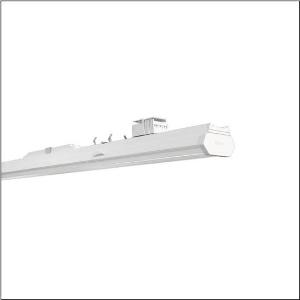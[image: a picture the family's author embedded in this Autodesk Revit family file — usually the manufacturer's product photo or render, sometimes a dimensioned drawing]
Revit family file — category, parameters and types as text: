
# Revit family: licross_r__11_protected_mo_51tp117n485g_c591
name_source: partatom
category: Lighting Fixtures
units: mm (PartAtom-declared; Revit-internal decimal feet)

## family parameters
Cut with Voids When Loaded = No
Host = Face
Light Source = No
Part Type = Normal
Room Calculation Point = No
Round Connector Dimension = Use Diameter
Shared = No

## types (1)
- Licross® 11 Protected MO (1 x LED, 8680 lm, 48.6 W, 4000K)
    Apparent Load = 49 VA
    CIE Flux Codes = 83 94 98 100 100
    Color Rendering = 80
    Color Temperature = 4000K
    Default Elevation = 1800 mm
    Description = Licross® 11 Protected MO, luminaire insert, of sheet steel, galvanised, coil coated, white, length: 1.500mm, width: 90mm, height: 101mm, LED rated luminous flux: 8.680lm, light colour: 840, control gear: ON/OFF, with plug, 3-pole, with phase selection, mains connection: 220..240V, AC, 50/60Hz, rated input power: 49W, halogen-free wiring, primary light control with lens, of plastic, primary optical cover: cover, of PMMA, light emission: direct distribution, primary light characteristic: symmetric, protection rating (complete): IP64, insulation class (complete): insulation class I (protective earthing), certification: CE, ENEC, VDE, UKCA, protection symbol: D if used in an environment with conductive dust loads with corresponding accessories, impact resistance: IK06, permissible ambient temperature for indoor applications: -25..+35°C, corresponds to IFS (International Featured Standards) requirements for safety and quality in the food industry, reducing of maximum allowable ambient temperature of 5°C with ceiling mounting, LABS conformity tested according to VDMA 24364:2018-05, packaging unit: 1 piece
    Height = 92 mm
    Lamp = 1 x LED
    Lamp Light Flux = 8680 lm
    Lamp Power = 48.6 W
    Lamp count = 1
    Length = 1500 mm
    Luminous efficacy = 179 lm/W
    Manufacturer = Siteco
    ModVariant = No
    Model = 51TP117N485G
    Mounting Place = Ceiling
    Mounting Type = Pendant
    Number of Poles = 1
    OnlyDefault = Yes
    Power Factor = 1
    Product Name = Licross® 11 Protected MO
    Product group = luminaire insert
    ProductGroupID = 901
    Protection Class = Protection class I
    Protection Degree = IP 64
    RLX_Detail_Level = 1
    RLX_Emergency_Light_Flux = 0 lm
    RLX_Emergency_Type = 0
    RLX_Emergency_Type_DB = No
    RlxData = <blob elided: 20365 chars, md5=6aeec92f>
    Socket = socket
    Standby Power = 0 W
    System Light Flux = 8680 lm
    System Power = 49 W
    Type Comments = Product without accessories
    Type Image = l_1256148.jpg
    URL = http://relux.com
    VarID = ---
    Voltage = 0 V
    Weight = 0.00 kg
    Width = 88 mm

## geometry (parser evidence)
native form markers: Blend x4, Sweep x9
no freeform markers — native parametric forms only
